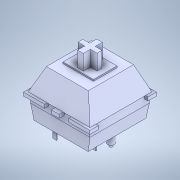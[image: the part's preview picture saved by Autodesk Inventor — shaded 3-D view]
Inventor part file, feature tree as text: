
AUTODESK INVENTOR PART (.ipt)
format: ipt  version: 2022 (Build 260153000, 153)  size: 169,984 bytes
history: native  units: in
note: dims shown in document units (in); Inventor stores cm internally (conversion verified against a paired STEP export)
features: chamfer x1
ambient origin geometry x8: Origin, YZ Plane, XZ Plane, XY Plane, X Axis, Y Axis, Z Axis, Center Point
bodies: Solid1 (feature_tree)
feature tree (1):
  chamfer  "Chamfer1"  [1 undecoded]
note: 1 required parameter value undecoded (feature->parameter linkage not recoverable at this tier; creation-order binding heuristic only, values carry confidence <= 0.55)
